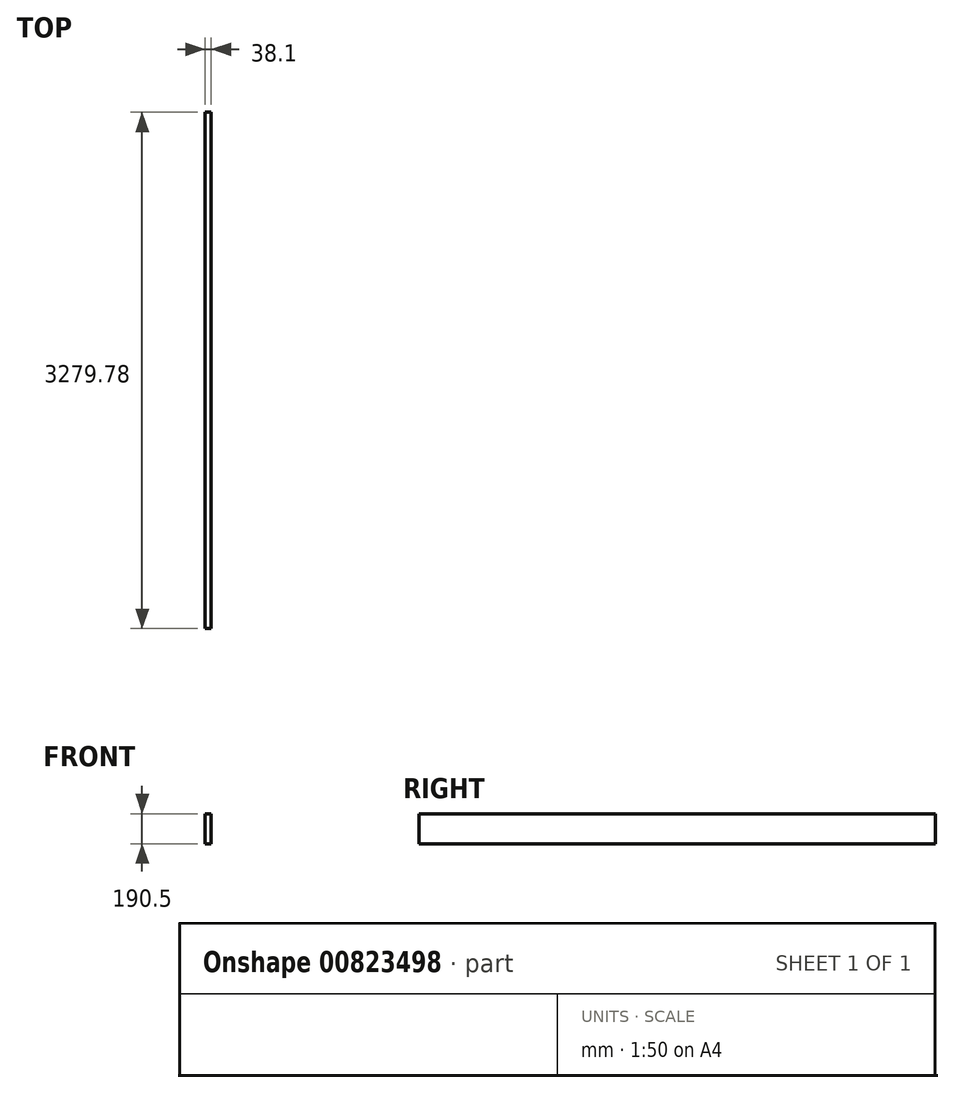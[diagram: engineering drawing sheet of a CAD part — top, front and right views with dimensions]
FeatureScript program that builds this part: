
annotation { "Feature Type Name" : "Feature", "Feature Type Description" : "" }
export const myFeature = defineFeature(function(context is Context, id is Id, definition is map)
    precondition{}
    {
        {
            var Q0;
            Q0=qCreatedBy(makeId("Front.planeOp"),FACE);
            var sketch = newSketch(context, id + "F0", { "sketchPlane" : qUnion([Q0])});
            skLineSegment(sketch, "E0.bottom", {"start": v(0, 0) * mm, "end": v(38.1, 0) * mm});
            skLineSegment(sketch, "E0.top", {"start": v(0, 190.5) * mm, "end": v(38.1, 190.5) * mm});
            skLineSegment(sketch, "E0.left", {"start": v(0, 0) * mm, "end": v(0, 190.5) * mm});
            skLineSegment(sketch, "E0.right", {"start": v(38.1, 0) * mm, "end": v(38.1, 190.5) * mm});
            skSolve(sketch);
        }
        {
            var Q0;
            Q0=qSketchRegion(id+"F0",true);
            extrude(context, id + "F1", {"entities" : qUnion([Q0]), "depth" : 3279.77 * mm, "offsetDistance" : 25.4 * mm});
        }
    });
